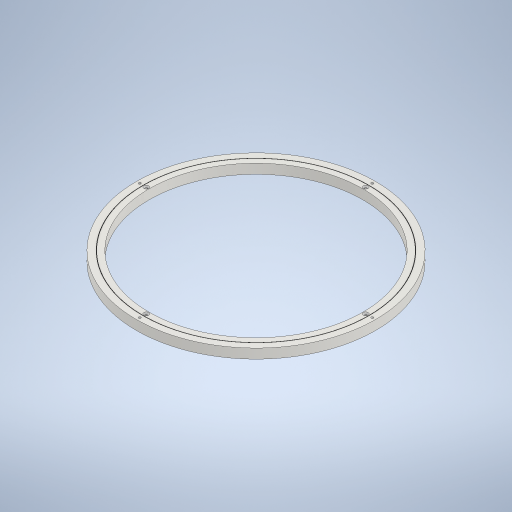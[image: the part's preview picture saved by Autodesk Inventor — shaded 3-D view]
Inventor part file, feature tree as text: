
AUTODESK INVENTOR PART (.ipt)
format: ipt  version: 2023 (Build 270158000, 158)  size: 287,232 bytes
history: native  units: in
note: dims shown in document units (in); Inventor stores cm internally (conversion verified against a paired STEP export)
features: sketch x2, hole x2, extrude x1
ambient origin geometry x8: Origin, YZ Plane, XZ Plane, XY Plane, X Axis, Y Axis, Z Axis, Center Point
bodies: Solid1 (feature_tree)
feature tree (5):
  sketch  "Sketch1"  dims[d0=8.7992in d1=9.8425in]
  extrude  "Extrusion1"  Depth=9.8425in
  hole  "Hole3"  [1 undecoded]
  hole  "Hole4"  [1 undecoded]
  sketch  "Sketch3"  dims[d2=9.2717in d3=9.311in d8=0.3937in d9=0.0in d32=1.5748in d34=360.0deg d36=0.0945in d37=0.2362in d38=0.1969in d39=0.0787in d40=90.0deg d41=0.315in d42=0.8108in d43=0.0945in d44=0.2362in d45=0.1969in d46=0.0787in d47=90.0deg d48=0.315in d49=0.8108in]
note: 2 required parameter values undecoded (feature->parameter linkage not recoverable at this tier; creation-order binding heuristic only, values carry confidence <= 0.55)
